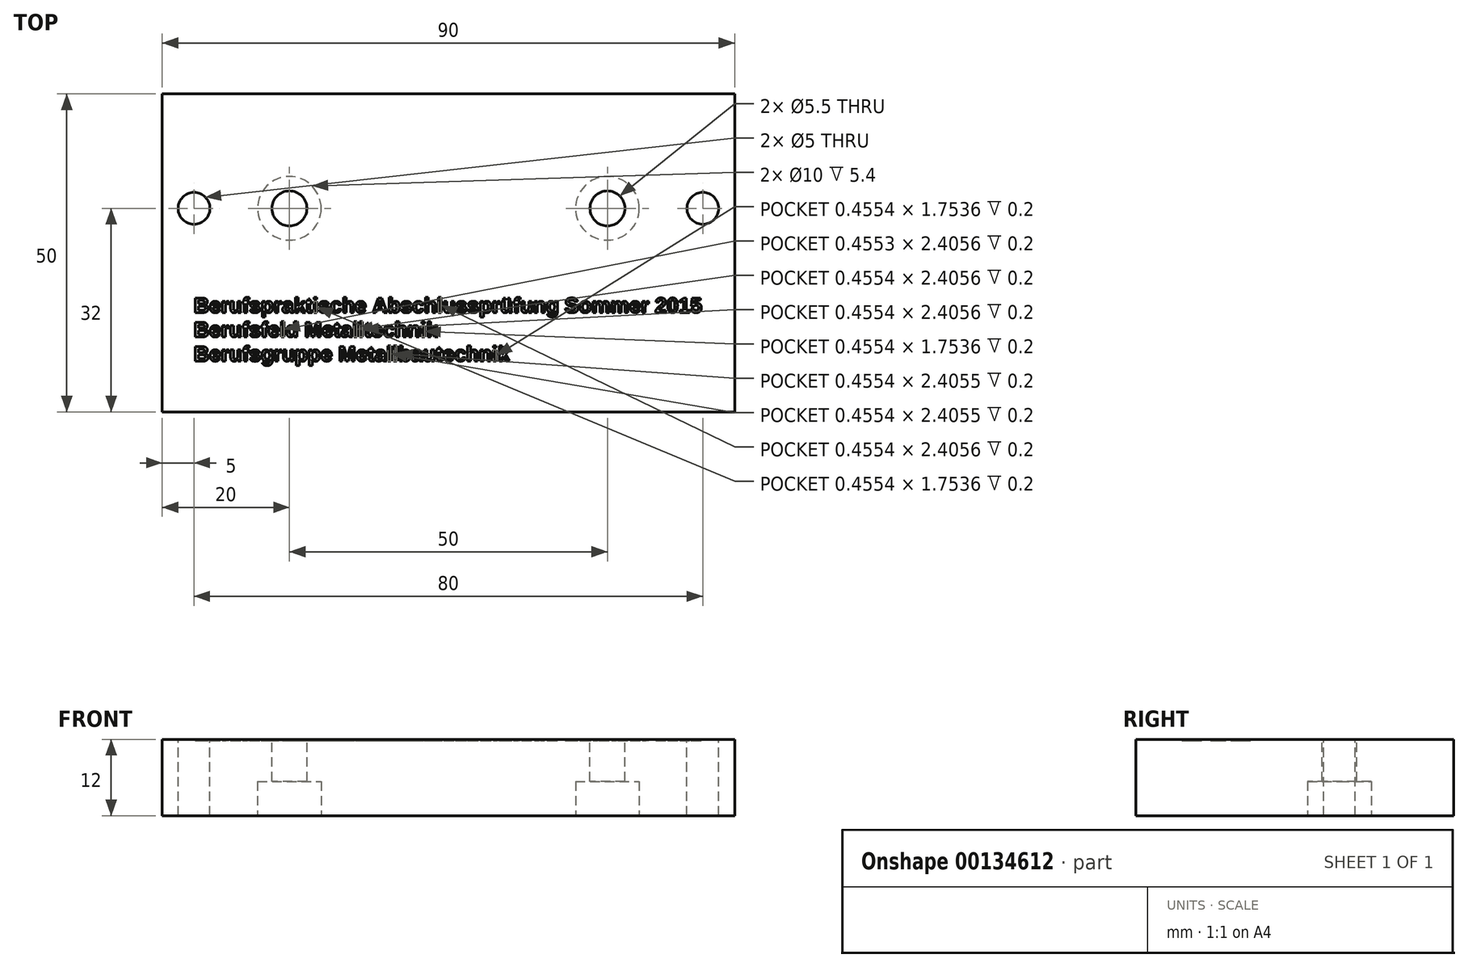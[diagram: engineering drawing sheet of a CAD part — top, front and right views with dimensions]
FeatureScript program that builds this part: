
annotation { "Feature Type Name" : "Feature", "Feature Type Description" : "" }
export const myFeature = defineFeature(function(context is Context, id is Id, definition is map)
    precondition{}
    {
        {
            var Q0;
            Q0=qCreatedBy(makeId("Top.planeOp"),FACE);
            var sketch = newSketch(context, id + "F0", { "sketchPlane" : qUnion([Q0])});
            skLineSegment(sketch, "E0.bottom", {"start": v(45, -25) * mm, "end": v(-45, -25) * mm});
            skLineSegment(sketch, "E0.top", {"start": v(45, 25) * mm, "end": v(-45, 25) * mm});
            skLineSegment(sketch, "E0.left", {"start": v(45, -25) * mm, "end": v(45, 25) * mm});
            skLineSegment(sketch, "E0.right", {"start": v(-45, -25) * mm, "end": v(-45, 25) * mm});
            skPoint(sketch, "E0.middle", {"position": v(0, 0) * mm});
            skSolve(sketch);
        }
        {
            var Q0;
            Q0=makeQuery(id+"F0.imprint","IMPRINT",FACE,{"disambiguationData":[TD([[makeQuery(id+"F0.imprint","IMPRINT",EDGE,{"derivedFrom":sQuery(id+"F0.wireOp",EDGE,"E0.bottom")}),-1.0]])]});
            extrude(context, id + "F1", {"entities" : qUnion([Q0]), "depth" : 12 * mm});
        }
        {
            var Q0;
            Q0=makeQuery(id+"F1.opExtrude","CAP_FACE",FACE,{"disambiguationData":[OSD([sQuery(id+"F0.wireOp",EDGE,"E0.bottom"),sQuery(id+"F0.wireOp",EDGE,"E0.top"),sQuery(id+"F0.wireOp",EDGE,"E0.left"),sQuery(id+"F0.wireOp",EDGE,"E0.right")])],"isStart":false});
            var sketch = newSketch(context, id + "F2", { "sketchPlane" : qUnion([Q0])});
            skCircle(sketch, "E1", {"center": v(-40, 7) * mm, "radius": 2.5 * mm});
            skCircle(sketch, "E2", {"center": v(-25, 7) * mm, "radius": 2.75 * mm});
            skCircle(sketch, "E3", {"center": v(25, 7) * mm, "radius": 2.75 * mm});
            skCircle(sketch, "E4", {"center": v(40, 7) * mm, "radius": 2.5 * mm});
            skLineSegment(sketch, "E5", {"start": v(-25, 7) * mm, "end": v(25, 7) * mm});
            skPoint(sketch, "E6", {"position": v(0, 25) * mm});
            skPoint(sketch, "E7", {"position": v(0, 7) * mm});
            skSolve(sketch);
        }
        {
            var Q0;
            Q0=makeQuery(id+"F2.imprint","IMPRINT",FACE,{"disambiguationData":[TD([[makeQuery(id+"F2.imprint","IMPRINT",EDGE,{"derivedFrom":sQuery(id+"F2.wireOp",EDGE,"E1")}),1.0]])]});
            var Q1;
            Q1=makeQuery(id+"F2.imprint","IMPRINT",FACE,{"disambiguationData":[TD([[makeQuery(id+"F2.imprint","IMPRINT",EDGE,{"derivedFrom":sQuery(id+"F2.wireOp",EDGE,"E2")}),1.0]])]});
            var Q2;
            Q2=makeQuery(id+"F2.imprint","IMPRINT",FACE,{"disambiguationData":[TD([[makeQuery(id+"F2.imprint","IMPRINT",EDGE,{"derivedFrom":sQuery(id+"F2.wireOp",EDGE,"E3")}),1.0]])]});
            var Q3;
            Q3=makeQuery(id+"F2.imprint","IMPRINT",FACE,{"disambiguationData":[TD([[makeQuery(id+"F2.imprint","IMPRINT",EDGE,{"derivedFrom":sQuery(id+"F2.wireOp",EDGE,"E4")}),1.0]])]});
            extrude(context, id + "F3", {"entities" : qUnion([Q0, Q1, Q2, Q3]), "operationType" : NewBodyOperationType.REMOVE, "oppositeDirection" : true, "depth" : 25 * mm});
        }
        {
            var Q0;
            Q0=makeQuery(id+"F1.opExtrude","CAP_FACE",FACE,{"disambiguationData":[OSD([sQuery(id+"F0.wireOp",EDGE,"E0.bottom"),sQuery(id+"F0.wireOp",EDGE,"E0.top"),sQuery(id+"F0.wireOp",EDGE,"E0.left"),sQuery(id+"F0.wireOp",EDGE,"E0.right")])],"isStart":true});
            var sketch = newSketch(context, id + "F4", { "sketchPlane" : qUnion([Q0])});
            skCircle(sketch, "E8", {"center": v(-25, -7) * mm, "radius": 5 * mm});
            skCircle(sketch, "E9", {"center": v(25, -7) * mm, "radius": 5 * mm});
            skSolve(sketch);
        }
        {
            var Q0;
            Q0=makeQuery(id+"F4.imprint","IMPRINT",FACE,{"disambiguationData":[TD([[makeQuery(id+"F4.imprint","IMPRINT",EDGE,{"derivedFrom":sQuery(id+"F4.wireOp",EDGE,"E8")}),1.0]])]});
            var Q1;
            Q1=makeQuery(id+"F4.imprint","IMPRINT",FACE,{"disambiguationData":[TD([[makeQuery(id+"F4.imprint","IMPRINT",EDGE,{"derivedFrom":sQuery(id+"F4.wireOp",EDGE,"E9")}),1.0]])]});
            extrude(context, id + "F5", {"entities" : qUnion([Q0, Q1]), "operationType" : NewBodyOperationType.REMOVE, "oppositeDirection" : true, "depth" : 5.4 * mm});
        }
        {
            var Q0;
            Q0=makeQuery(id+"F1.opExtrude","CAP_FACE",FACE,{"disambiguationData":[OSD([sQuery(id+"F0.wireOp",EDGE,"E0.bottom"),sQuery(id+"F0.wireOp",EDGE,"E0.top"),sQuery(id+"F0.wireOp",EDGE,"E0.left"),sQuery(id+"F0.wireOp",EDGE,"E0.right")])],"isStart":false});
            var sketch = newSketch(context, id + "F6", { "sketchPlane" : qUnion([Q0])});
            skText(sketch, "E10", { "text": "Berufspraktische Abschlussprüfung Sommer 2015\nBerufsfeld Metalltechnik\nBerufsgruppe Metallbautechnik", "fontName": "Arimo-Bold.ttf"});
            const initialGuessF6  = {"E10": [-0.04, -0.00939, 1, 0, 0.00239]};
            skSetInitialGuess(sketch, initialGuessF6);
            skSolve(sketch);
        }
        {
            var Q0;
            Q0 = qSketchRegion(id + "F6", true);
            extrude(context, id + "F7", {"entities" : qUnion([Q0]), "operationType" : NewBodyOperationType.REMOVE, "oppositeDirection" : true, "depth" : 0.2 * mm});
        }
    });
